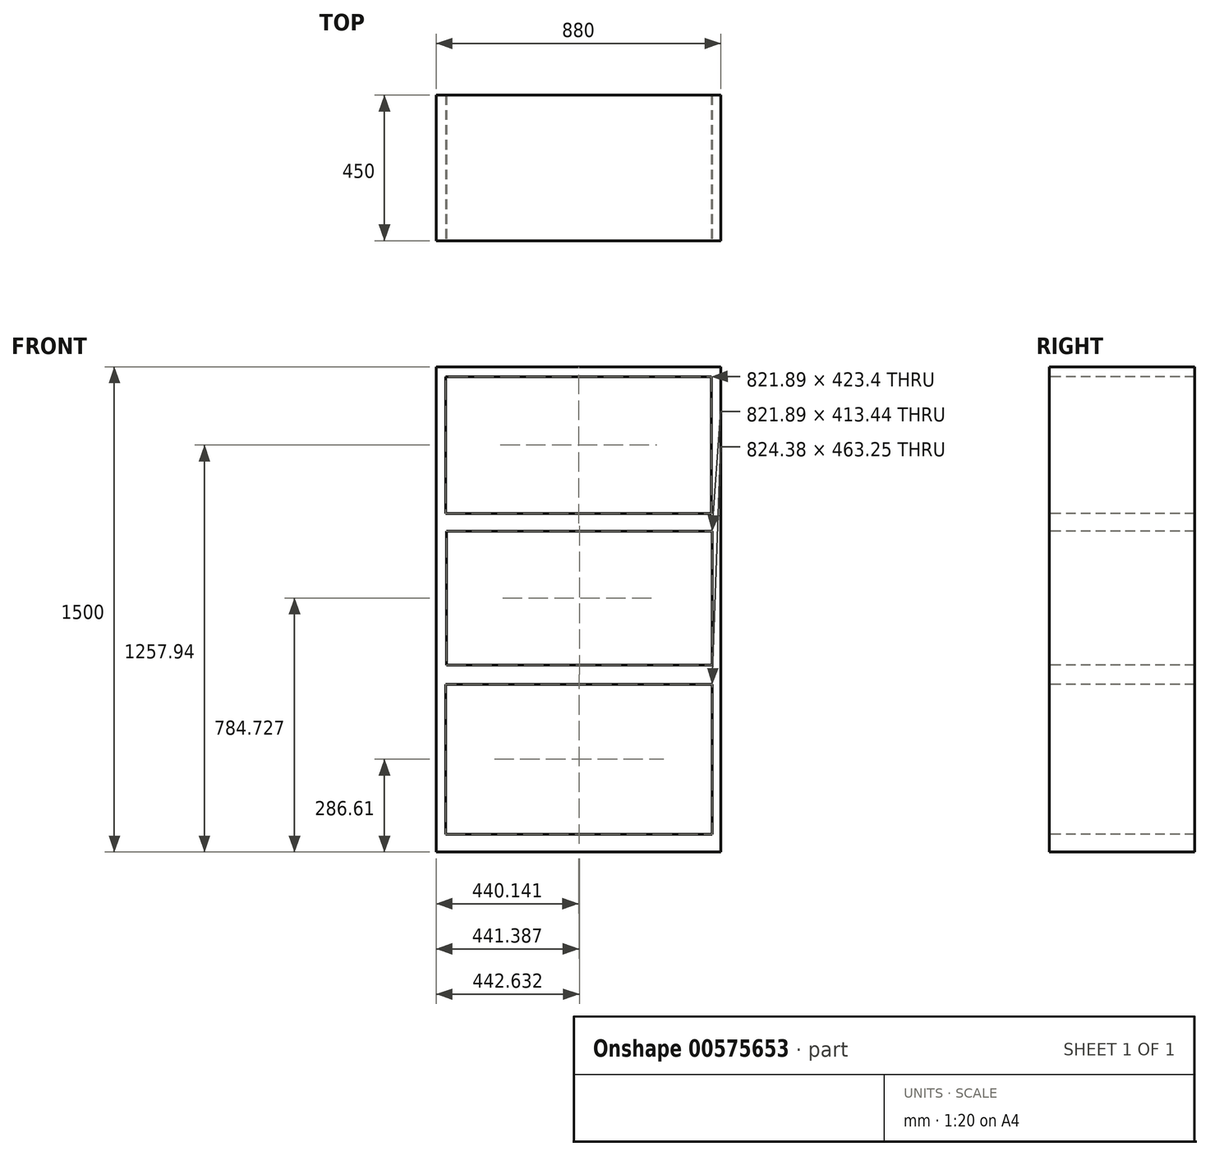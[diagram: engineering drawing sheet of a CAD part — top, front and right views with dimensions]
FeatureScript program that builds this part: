
annotation { "Feature Type Name" : "Feature", "Feature Type Description" : "" }
export const myFeature = defineFeature(function(context is Context, id is Id, definition is map)
    precondition{}
    {
        {
            var Q0;
            Q0=qCreatedBy(makeId("Top.planeOp"),FACE);
            var sketch = newSketch(context, id + "F0", { "sketchPlane" : qUnion([Q0])});
            skLineSegment(sketch, "E0.bottom", {"start": v(0, 0) * mm, "end": v(-880, 0) * mm});
            skLineSegment(sketch, "E0.top", {"start": v(0, 450) * mm, "end": v(-880, 450) * mm});
            skLineSegment(sketch, "E0.left", {"start": v(0, 0) * mm, "end": v(0, 450) * mm});
            skLineSegment(sketch, "E0.right", {"start": v(-880, 0) * mm, "end": v(-880, 450) * mm});
            skSolve(sketch);
        }
        {
            var Q0;
            Q0 = qSketchRegion(id + "F0", true);
            extrude(context, id + "F1", {"entities" : qUnion([Q0]), "depth" : 1500 * mm, "offsetDistance" : 25 * mm});
        }
        {
            var Q0;
            Q0=makeQuery(id+"F1.opExtrude","SWEPT_FACE",FACE,{"disambiguationData":[OSD([sQuery(id+"F0.wireOp",EDGE,"E0.bottom")])]});
            var sketch = newSketch(context, id + "F2", { "sketchPlane" : qUnion([Q0])});
            skLineSegment(sketch, "E1.bottom", {"start": v(-850.8, 1469.64) * mm, "end": v(-28.91, 1469.64) * mm});
            skLineSegment(sketch, "E1.top", {"start": v(-850.8, 1046.24) * mm, "end": v(-28.91, 1046.24) * mm});
            skLineSegment(sketch, "E1.left", {"start": v(-850.8, 1469.64) * mm, "end": v(-850.8, 1046.24) * mm});
            skLineSegment(sketch, "E1.right", {"start": v(-28.91, 1469.64) * mm, "end": v(-28.91, 1046.24) * mm});
            skLineSegment(sketch, "E2.bottom", {"start": v(-848.32, 991.45) * mm, "end": v(-26.42, 991.45) * mm});
            skLineSegment(sketch, "E2.top", {"start": v(-848.32, 578) * mm, "end": v(-26.42, 578) * mm});
            skLineSegment(sketch, "E2.left", {"start": v(-848.32, 991.45) * mm, "end": v(-848.32, 578) * mm});
            skLineSegment(sketch, "E2.right", {"start": v(-26.42, 991.45) * mm, "end": v(-26.42, 578) * mm});
            skLineSegment(sketch, "E3.bottom", {"start": v(-850.8, 518.23) * mm, "end": v(-26.42, 518.23) * mm});
            skLineSegment(sketch, "E3.top", {"start": v(-850.8, 54.98) * mm, "end": v(-26.42, 54.98) * mm});
            skLineSegment(sketch, "E3.left", {"start": v(-850.8, 518.23) * mm, "end": v(-850.8, 54.98) * mm});
            skLineSegment(sketch, "E3.right", {"start": v(-26.42, 518.23) * mm, "end": v(-26.42, 54.98) * mm});
            skSolve(sketch);
        }
        {
            var Q0;
            Q0 = qSketchRegion(id + "F2", true);
            extrude(context, id + "F3", {"entities" : qUnion([Q0]), "operationType" : NewBodyOperationType.REMOVE, "endBound" : BoundingType.UP_TO_NEXT, "oppositeDirection" : true, "depth" : 25 * mm, "offsetDistance" : 25 * mm});
        }
    });
